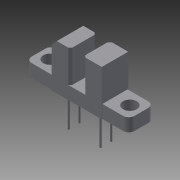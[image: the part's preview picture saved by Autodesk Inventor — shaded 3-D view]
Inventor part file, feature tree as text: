
AUTODESK INVENTOR PART (.ipt)
format: ipt  version: 2015 SP1 (Build 190203100, 203)  size: 144,896 bytes
history: native  units: mm
features: extrude x4, sketch x4, fillet x1, mirror x1, chamfer x1
ambient origin geometry x8: Origin, YZ Plane, XZ Plane, XY Plane, X Axis, Y Axis, Z Axis, Center Point
bodies: Solid1 (feature_tree)
feature tree (11):
  extrude  "Extrusion1"  Depth=10.8mm
  extrude  "Extrusion2"  Depth=3.1mm
  fillet  "Fillet1"  Radius=3.1mm
  extrude  "Extrusion3"  Depth=1.2mm
  extrude  "Extrusion4"  Depth=6.3mm TaperAngle=0.0deg
  mirror  "Mirror1"
  chamfer  "Chamfer1"  Distance=6.0mm
  sketch  "Sketch1"  dims[d0=11.9mm d1=10.8mm]
  sketch  "Sketch2"  dims[d2=2.6mm d3=3.1mm d4=3.1mm]
  sketch  "Sketch3"  dims[d5=135.0deg d6=1.2mm]
  sketch  "Sketch4"  dims[d7=6.3mm d8=0.0mm d10=6.3mm d11=0.0mm d12=6.0mm d13=3.1mm d14=1.35mm d15=3.3mm d16=3.55mm d17=6.3mm d18=0.0mm d19=0.4mm d20=3.8mm d21=0.4mm d22=2.54mm d23=7.8mm d24=0.0mm d25=0.5mm d26=2.0mm d27=45.0deg]
